# Revit family: QF_ELECTROLUXPROFESSIONAL_1LSNSR_TD6-16_S
name_source: partatom
category: Attrezzature speciali
units: mm (PartAtom-declared; Revit-internal decimal feet)

## family parameters
Basato su piano di lavoro = No
Condiviso = No
Punto di calcolo locali = No
Quota connettore circolare = Usa diametro
Sempre verticale = Sì
Taglio con vuoti quando caricato = No
Tipo di parte = Normale

## types (3) — shared parameters
Cycle = 50 Hz
Depth Actual = 1360 mm  [stored 4.46194 ft]
Height Actual = 1690 mm  [stored 5.54462 ft]
Latent Heat Output = 0.0
Length Actual = 715 mm  [stored 2.3458 ft]
Modello = TD6-16
Produttore = Electrolux Professional
Sensible Heat Output = 0.0
Steam Pounds per Hour = 41
URL = www.electroluxprofessional.com
Watts = 800 W
Weight = 203
zero-valued in all types: Gas KW, Prospetto di default

## per-type parameters (varying)
| type | Descrizione | Item Number | Phase | Volts |
| 9872230022 | TUMBLE DRYER TD6-16 16KG GALVA.DRUM STEAM 25KW 240/50/1 COMPASS PRO 6G81 SLVR/SLVR DO.RIGHT REV MB STOP DMPR | 1L0G4E | 1 | 240 V |
| 9872230053 | TUMBLE DRYER TD6-16 16KG GALVA.DRUM STEAM 25KW 380-415/50/3N COMPASS PRO 6G82 SLVR/SLVR DO.RIGHT REV DISCON DMPR | 1L0GFW | 3 | 415 V |
| 9872230052 | TUMBLE DRYER TD6-16 16KG GALVA.DRUM STEAM 25KW 230/50/1 COMPASS PRO 6G81 SLVR/SLVR DO.RIGHT REV MB DISCON DMPR | 1LSPBL | 1 | 230 V |

note: [stored X ft] marks values corroborated as IEEE doubles in the binary element streams (Revit-internal decimal feet)

## geometry (parser evidence)
native form markers: Blend x8
no freeform markers — native parametric forms only
